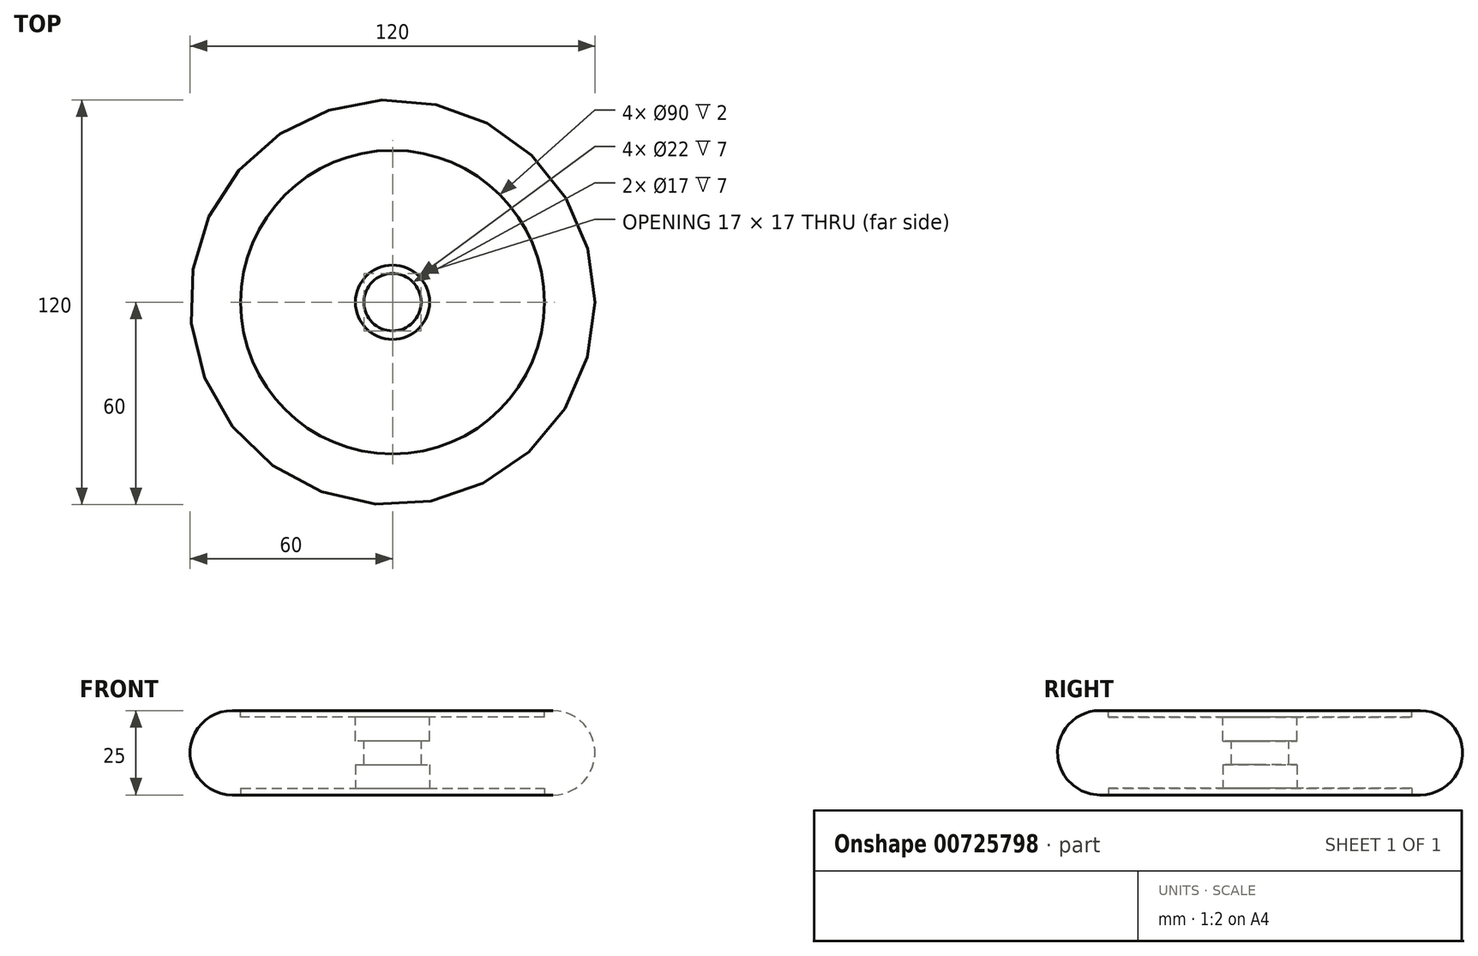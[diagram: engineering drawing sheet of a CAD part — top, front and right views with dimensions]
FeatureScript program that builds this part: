
annotation { "Feature Type Name" : "Feature", "Feature Type Description" : "" }
export const myFeature = defineFeature(function(context is Context, id is Id, definition is map)
    precondition{}
    {
        {
            var Q0;
            Q0=qCreatedBy(makeId("Top.planeOp"),FACE);
            var sketch = newSketch(context, id + "F0", { "sketchPlane" : qUnion([Q0])});
            skCircle(sketch, "E0", {"center": v(0, 0) * mm, "radius": 60 * mm});
            skSolve(sketch);
        }
        {
            var Q0;
            Q0=makeQuery(id+"F0.imprint","IMPRINT",FACE,{"disambiguationData":[TD([[makeQuery(id+"F0.imprint","IMPRINT",EDGE,{"derivedFrom":sQuery(id+"F0.wireOp",EDGE,"E0")}),1.0]])]});
            extrude(context, id + "F1", {"entities" : qUnion([Q0]), "depth" : 25 * mm});
        }
        {
            var Q0;
            Q0=makeQuery(id+"F1.opExtrude","CAP_FACE",FACE,{"disambiguationData":[OSD([sQuery(id+"F0.wireOp",EDGE,"E0")])],"isStart":false});
            var sketch = newSketch(context, id + "F2", { "sketchPlane" : qUnion([Q0])});
            skCircle(sketch, "E1", {"center": v(0, 0) * mm, "radius": 11 * mm});
            skSolve(sketch);
        }
        {
            var Q0;
            Q0=makeQuery(id+"F2.imprint","IMPRINT",FACE,{"disambiguationData":[TD([[makeQuery(id+"F2.imprint","IMPRINT",EDGE,{"derivedFrom":sQuery(id+"F2.wireOp",EDGE,"E1")}),-1.0]])]});
            var sketch = newSketch(context, id + "F3", { "sketchPlane" : qUnion([Q0])});
            skCircle(sketch, "E2", {"center": v(0, 0) * mm, "radius": 45 * mm});
            skSolve(sketch);
        }
        {
            var Q0;
            Q0=qSketchRegion(id+"F2",true);
            extrude(context, id + "F4", {"entities" : qUnion([Q0]), "operationType" : NewBodyOperationType.REMOVE, "oppositeDirection" : true, "depth" : 9 * mm});
        }
        {
            var Q0;
            Q0=makeQuery(id+"F3.imprint","IMPRINT",FACE,{"disambiguationData":[TD([[makeQuery(id+"F3.imprint","IMPRINT",EDGE,{"derivedFrom":sQuery(id+"F3.wireOp",EDGE,"E2")}),1.0]])]});
            extrude(context, id + "F5", {"entities" : qUnion([Q0]), "operationType" : NewBodyOperationType.REMOVE, "oppositeDirection" : true, "depth" : 0.01 * mm});
        }
        {
            var Q0;
            Q0=qSketchRegion(id+"F3",true);
            extrude(context, id + "F6", {"entities" : qUnion([Q0]), "operationType" : NewBodyOperationType.REMOVE, "oppositeDirection" : true, "depth" : 2 * mm});
        }
        {
            var Q0;
            Q0=makeQuery(id+"F1.opExtrude","CAP_FACE",FACE,{"disambiguationData":[OSD([sQuery(id+"F0.wireOp",EDGE,"E0")])],"isStart":true});
            var sketch = newSketch(context, id + "F7", { "sketchPlane" : qUnion([Q0])});
            skCircle(sketch, "E3", {"center": v(0, 0) * mm, "radius": 11 * mm});
            skSolve(sketch);
        }
        {
            var Q0;
            Q0=makeQuery(id+"F7.imprint","IMPRINT",FACE,{"disambiguationData":[TD([[makeQuery(id+"F7.imprint","IMPRINT",EDGE,{"derivedFrom":sQuery(id+"F7.wireOp",EDGE,"E3")}),-1.0]])]});
            var sketch = newSketch(context, id + "F8", { "sketchPlane" : qUnion([Q0])});
            skCircle(sketch, "E4", {"center": v(0, 0) * mm, "radius": 45 * mm});
            skSolve(sketch);
        }
        {
            var Q0;
            Q0=qSketchRegion(id+"F7",true);
            extrude(context, id + "F9", {"entities" : qUnion([Q0]), "operationType" : NewBodyOperationType.REMOVE, "oppositeDirection" : true, "depth" : 9 * mm});
        }
        {
            var Q0;
            Q0=qSketchRegion(id+"F8",true);
            extrude(context, id + "F10", {"entities" : qUnion([Q0]), "operationType" : NewBodyOperationType.REMOVE, "oppositeDirection" : true, "depth" : 2 * mm});
        }
        {
            var Q0;
            Q0=makeQuery(id+"F1.opExtrude","CAP_EDGE",EDGE,{"disambiguationData":[OSD([sQuery(id+"F0.wireOp",EDGE,"E0")])],"isStart":false});
            fillet(context, id + "F11", {"entities" : qUnion([Q0]), "radius" : 12.5 * mm, "tangentPropagation" : true, "allowEdgeOverflow" : false});
        }
        {
            var Q0;
            Q0=makeQuery(id+"F1.opExtrude","CAP_EDGE",EDGE,{"disambiguationData":[OSD([sQuery(id+"F0.wireOp",EDGE,"E0")])],"isStart":true});
            fillet(context, id + "F12", {"entities" : qUnion([Q0]), "radius" : 12.5 * mm, "tangentPropagation" : true, "allowEdgeOverflow" : false});
        }
        {
            var Q0;
            Q0=makeQuery(id+"F4.boolean.opBoolean","COPY",FACE,{"derivedFrom":makeQuery(id+"F4.opExtrude","CAP_FACE",FACE,{"disambiguationData":[OSD([sQuery(id+"F2.wireOp",EDGE,"E1")])],"isStart":false})});
            var sketch = newSketch(context, id + "F13", { "sketchPlane" : qUnion([Q0])});
            skCircle(sketch, "E5", {"center": v(0, 0) * mm, "radius": 8.5 * mm});
            skSolve(sketch);
        }
        {
            var Q0;
            Q0=makeQuery(id+"F13.imprint","IMPRINT",FACE,{"disambiguationData":[TD([[makeQuery(id+"F13.imprint","IMPRINT",EDGE,{"derivedFrom":sQuery(id+"F13.wireOp",EDGE,"E5")}),1.0]])]});
            extrude(context, id + "F14", {"entities" : qUnion([Q0]), "operationType" : NewBodyOperationType.REMOVE, "oppositeDirection" : true, "depth" : 25 * mm});
        }
    });
